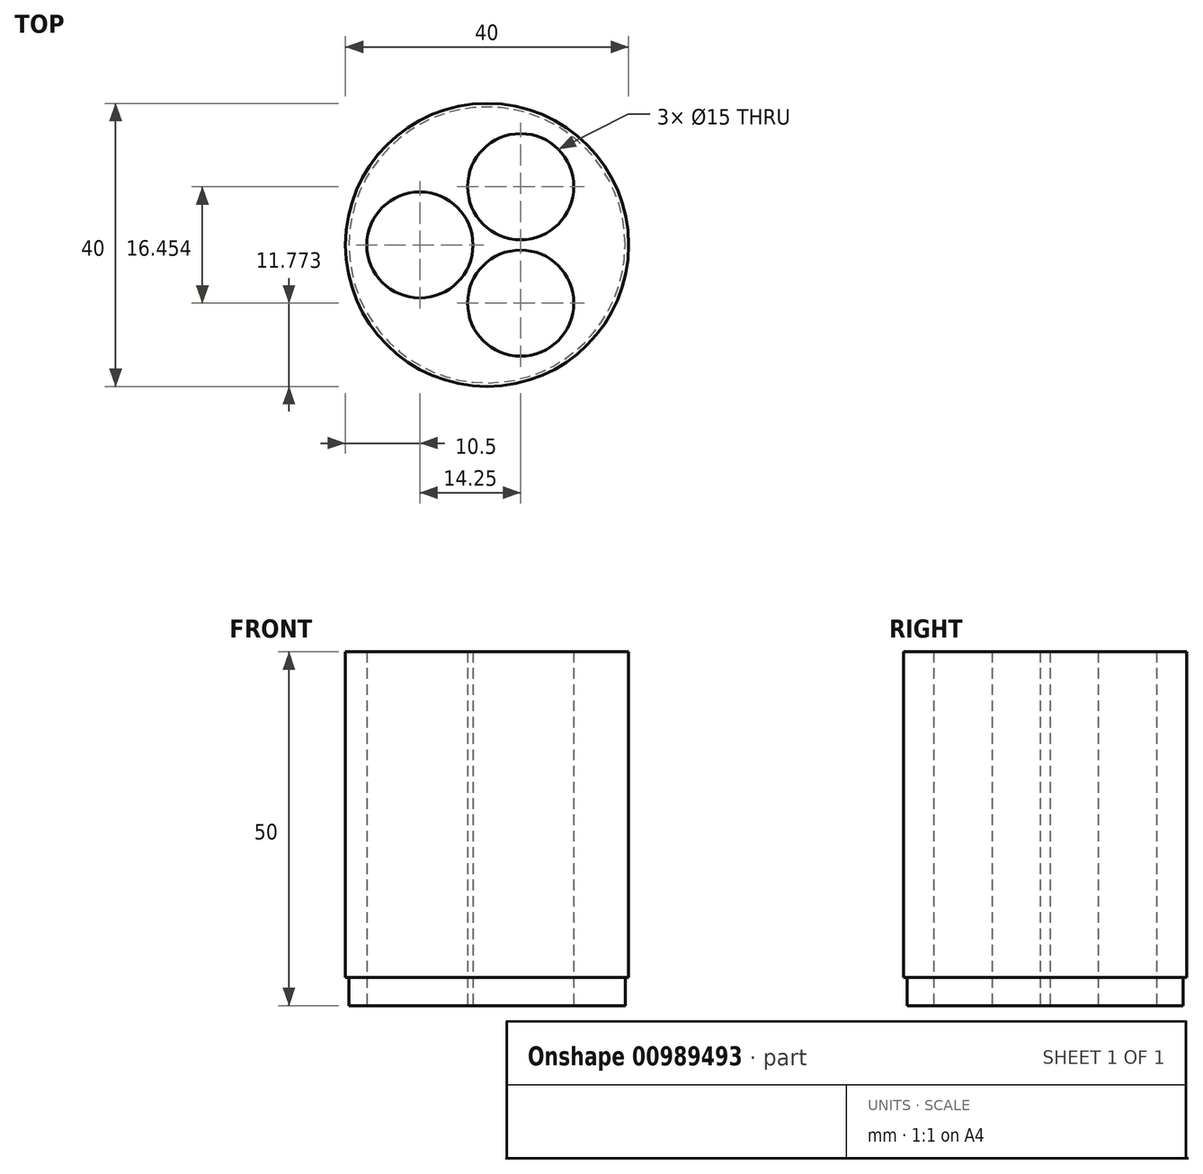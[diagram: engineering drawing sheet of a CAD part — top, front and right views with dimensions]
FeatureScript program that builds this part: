
annotation { "Feature Type Name" : "Feature", "Feature Type Description" : "" }
export const myFeature = defineFeature(function(context is Context, id is Id, definition is map)
    precondition{}
    {
        {
            var Q0;
            Q0=qCreatedBy(makeId("Top.planeOp"),FACE);
            var sketch = newSketch(context, id + "F0", { "sketchPlane" : qUnion([Q0])});
            skCircle(sketch, "E0", {"center": v(0, 0) * mm, "radius": 20 * mm});
            skSolve(sketch);
        }
        {
            var Q0;
            Q0 = qSketchRegion(id + "F0", true);
            extrude(context, id + "F1", {"entities" : qUnion([Q0]), "depth" : 50 * mm, "offsetDistance" : 25 * mm});
        }
        {
            var Q0;
            Q0=makeQuery(id+"F1.opExtrude","CAP_FACE",FACE,{"disambiguationData":[OSD([sQuery(id+"F0.wireOp",EDGE,"E0")])],"isStart":true});
            var sketch = newSketch(context, id + "F2", { "sketchPlane" : qUnion([Q0])});
            skCircle(sketch, "E1", {"center": v(-9.5, 0) * mm, "radius": 7.5 * mm});
            skCircle(sketch, "E2.1.0", {"center": v(4.75, -8.23) * mm, "radius": 7.5 * mm});
            skCircle(sketch, "E2.2.0", {"center": v(4.75, 8.23) * mm, "radius": 7.5 * mm});
            skPoint(sketch, "E2.center", {"position": v(0, 0) * mm});
            skSolve(sketch);
        }
        {
            var Q0;
            Q0 = qSketchRegion(id + "F2", true);
            extrude(context, id + "F3", {"entities" : qUnion([Q0]), "operationType" : NewBodyOperationType.REMOVE, "endBound" : BoundingType.THROUGH_ALL, "oppositeDirection" : true, "depth" : 25 * mm, "offsetDistance" : 25 * mm});
        }
        {
            var Q0;
            Q0=makeQuery(id+"F1.opExtrude","CAP_FACE",FACE,{"disambiguationData":[OSD([sQuery(id+"F0.wireOp",EDGE,"E0")])],"isStart":true});
            var sketch = newSketch(context, id + "F4", { "sketchPlane" : qUnion([Q0])});
            skCircle(sketch, "E3", {"center": v(0, 0) * mm, "radius": 19.5 * mm});
            skCircle(sketch, "E4", {"center": v(0, 0) * mm, "radius": 20 * mm});
            skSolve(sketch);
        }
        {
            var Q0;
            Q0 = qSketchRegion(id + "F4", true);
            extrude(context, id + "F5", {"entities" : qUnion([Q0]), "operationType" : NewBodyOperationType.REMOVE, "oppositeDirection" : true, "depth" : 4 * mm, "offsetDistance" : 25 * mm});
        }
    });
